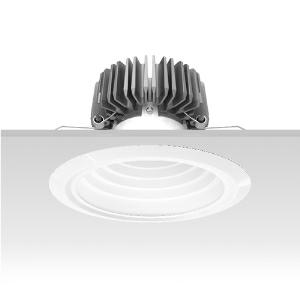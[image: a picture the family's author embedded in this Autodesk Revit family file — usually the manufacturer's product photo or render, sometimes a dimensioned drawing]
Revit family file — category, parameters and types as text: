
# Revit family: 3f_filippi_-_3f_reno_bianco_ampio_3f_filippi_-_30679_a01025_-_3f_reno_200_wh_3000-840_dali_wide___vt_wh_26f7
name_source: partatom
category: Lighting Fixtures
units: mm (PartAtom-declared; Revit-internal decimal feet)

## family parameters
Cut with Voids When Loaded = No
Host = Face
Light Source = No
Part Type = Normal
Room Calculation Point = No
Round Connector Dimension = Use Diameter
Shared = No

## types (1)
- 3F Filippi - 3F Reno Bianco Ampio (1 x LED, 2529 lm, 28 W, 4000 K)
    Apparent Load = 28 VA
    Approval mark = CE
    CIE Flux Codes = 75 94 99 100 100
    Color Rendering = 80
    Color Temperature = 4000 K
    Control Gear = Electronic transformer
    Default Elevation = 1800 mm
    Description = ILLUMINOTECHNICAL
Luminous efficiency 100% (DLOR 100%, ULOR 0%).
Initial luminous flux of the luminaire 2529 lm.
Direct symmetric wide distribution.
Installation Interdistance Transv.D = 1.56 x hu - Long.D = 1.56 x hu.
Tabular UGR (CIE 117 - 4H-8H; S=0.25H; 70/50/20): RUG 21.8 - 21.7.
Beam angle: 74° - 74°.
Luminous efficacy 90 lm/W.
Lifetime (L90/B10): 30000 h. (tq+25°C)
Lifetime (L85/B10): 50000 h. (tq+25°C)
Lifetime (L70/B10): 80000 h. (tq+25°C)
Sudden decreased luminous flux after 50000 hours: 0% (C0).
Photobiological safety in compliance with IEC/TR 62778: RG0 risk exempt, (IEC 62471).
In compliance with IEC/EN 62722-2-1 - IEC/EN 62717 standards.

SOURCE
Compact LED module 3000/840.
Energy efficiency class (UE 2019/2020 - UE 2019/2015): E.
CIE 13.3 Colour rendering index: CRI >80 (R9 <50%).
IES TM-30 Fidelity Index: Rf = 84 Rg = 95.
CCT nominal colour temperature 4000 K.
Colour initial tolerance (MacAdam): SDCM 3.
Zhaga Book 3 compliant.

MECHANICAL
Passive heat dissipator in die-casting aluminium, oversized, for optimum thermal management of the LED module.
Parabolic element with graduated/concentric rings in white polycarbonate.
Transparent external lens with glossy and satin differentiated surfaces, with a cooling and anti-insect system in methacrylate (PMMA).
Fastening spring clips in stainless steel.
Dimensions: diameter 226 mm, height 146 mm. Weight 1.755 kg.
IP44 protection degree for exposed part, IP20 for recessed part.
Mechanical strength to impacts IK06 (1 joule).
Glow-wire test resistance 650°C.

ELECTRICAL
Wiring on a separate unit.
Halogen Free DALI-2 DATI (Parts 251, 252, 253), PUSH-DIM, electronic wiring 230V-50/60Hz, power factor 0.97 at full load, THD <25%, constant output current, SELV, class II, 1 driver, 1 DALI addresse.
Power of the luminaire 28 W.
ENEC - CE.
SAFE FLICKER: PstLM=<1 and SVM=<0.4 (IEC TR 61547-1 and IEC TR 63158), to ensure a more comfortable and safe light.
Luminaire compliant with EN 60598-2-22 for power supply from a centralised emergency system CPSS (Central Power Supply System), not incorporated in the luminaire - high risk areas excluded. The default power and flux are 100% in AC and 100% in DC.
Ambient temperature from 0°C to +25°C.
Temperature class T6 max 85°C.
Relative humidity UR: <85%.

INSTALLATION
Pull-up recessed fitting.
False ceiling carving: 200 mm.
All accessories dedicated to this product are available on the Catalog and on our website www.3F-Filippi.com.

ACCESSORIES
A01025 - VT transparent glass, tempered, not flammable, locked and in line with the trim, in white polycarbonate.

APPLICATIONS
Environments: architectural, commercial, exhibition areas, transit areas, corridors, shops, display windows, service areas.
In false ceilings with narrow voids.

LIGHT MANAGEMENT
Recommended minimum setting: 10%.
The luminaire, equipped with (DALI-2 DATI) driver, can be controlled manually with 3F Easy Dim technology or automatically/manually with wired or wireless DALI/D2D control systems.
The D2D driver guarantees interoperability with other devices with the same certification by making the following information available:
Device Data (Part 251), Energy Report (Part 252), Diagnosis & Maintenance (Part 253).
In electrical systems without a regulation system (manual or automatic) and DALI bus, a suitable jumper must be made on the DA-DA terminals of the appliance.

WARNING
Luminaire designed for disposal/recycling at end-of-life.
Replaceable (LED only) light source by a professional. Replaceable control gear by a professional.
    Height = 0 mm  [stored 0 ft]
    Lamp = 1 x LED
    Lamp Light Flux = 2529 lm
    Lamp Power = 28 W
    Lamp count = 1
    Length = 226 mm
    Lifetime = 50000 h
    Luminous efficacy = 90 lm/W
    Manufacturer = 3F Filippi
    ModVariant = No
    Model = 3F Filippi - 30679+A01025 - 3F Reno 200 WH 3000-840 DALI WIDE + VT WH
    Mounting Place = Ceiling
    Mounting Type = Recessed
    Number of Poles = 1
    OnlyDefault = Yes
    Power Factor = 1
    Product Name = 3F Filippi - 3F Reno Bianco Ampio
    Product group = recessed luminaire
    ProductGroupID = 4
    Protection Class = Protection class II
    Protection Degree = IP 20
    RLX_Detail_Level = 1
    RLX_Emergency_Light_Flux = 0 lm
    RLX_Emergency_Type = 0
    RLX_Emergency_Type_DB = No
    RlxData = <blob elided: 97989 chars, md5=5c6f4ee2>
    Socket = socket
    Standby Power = 0 W
    System Light Flux = 2529 lm
    System Power = 28 W
    Type Comments = Product without accessories
    Type Image = 3ffilippi_3f_reno_200_wh__a01025.jpg
    URL = http://relux.com
    VarID = ---
    Voltage = 0 V
    Weight = 0.00 kg
    Width = 0 mm  [stored 0 ft]

note: [stored X ft] marks values corroborated as IEEE doubles in the binary element streams (Revit-internal decimal feet)

## geometry (parser evidence)
native form markers: Blend x4, Sweep x10
no freeform markers — native parametric forms only
